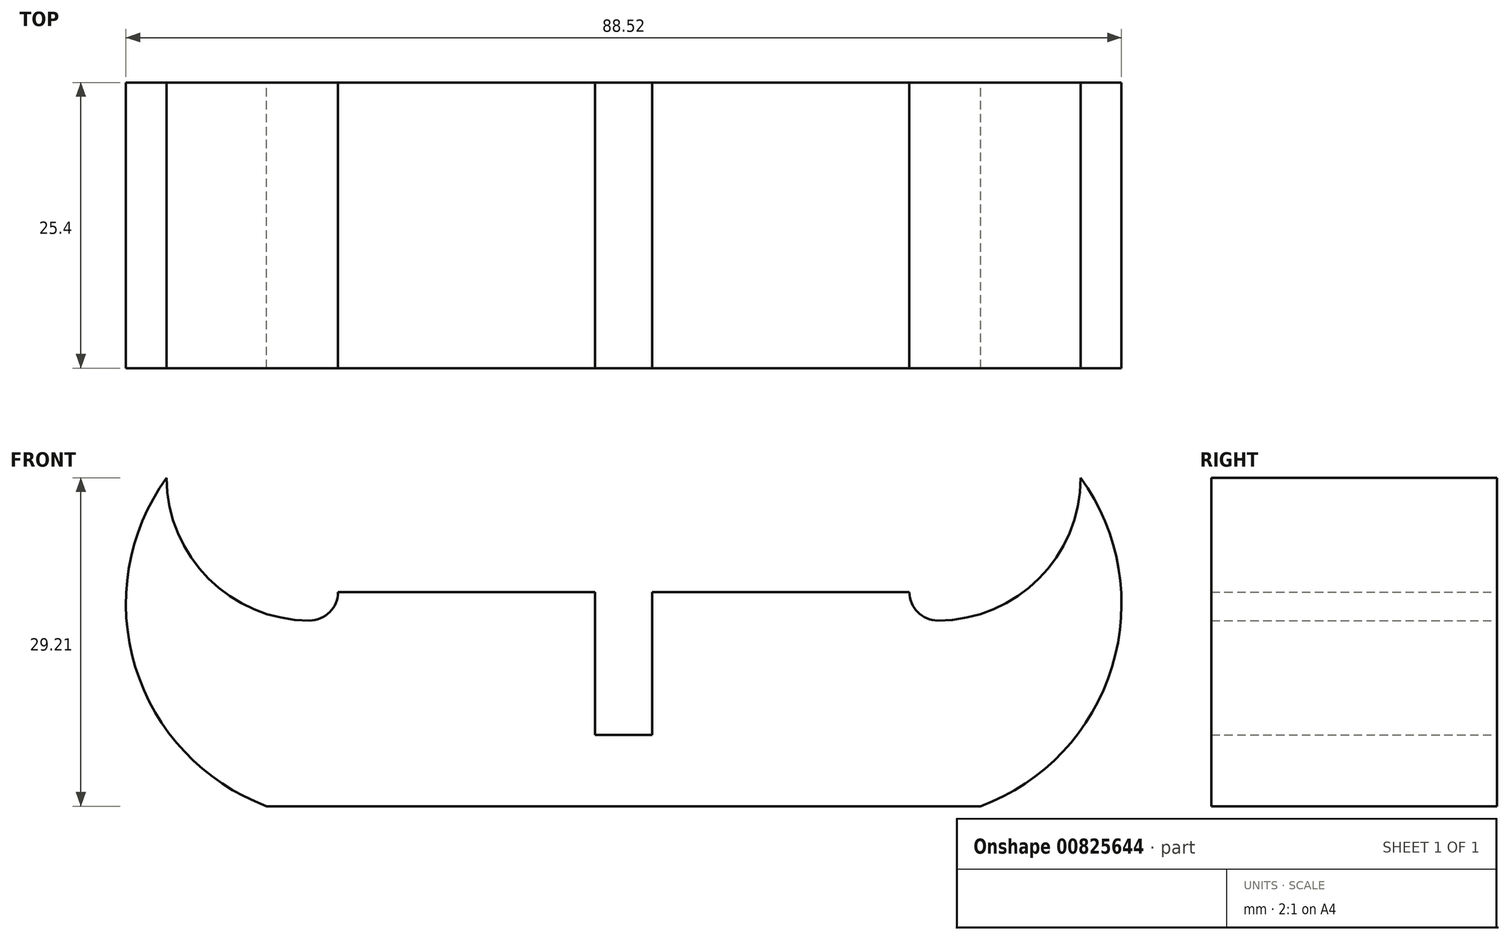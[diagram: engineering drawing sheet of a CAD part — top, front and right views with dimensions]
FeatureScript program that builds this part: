
annotation { "Feature Type Name" : "Feature", "Feature Type Description" : "" }
export const myFeature = defineFeature(function(context is Context, id is Id, definition is map)
    precondition{}
    {
        {
            var Q0;
            Q0=qCreatedBy(makeId("Front.planeOp"),FACE);
            var sketch = newSketch(context, id + "F0", { "sketchPlane" : qUnion([Q0])});
            skLineSegment(sketch, "E0", {"start": v(0, 0) * mm, "end": v(-19.05, 0) * mm});
            skLineSegment(sketch, "E1", {"start": v(-19.05, 0) * mm, "end": v(-19.05, -2.54) * mm});
            skLineSegment(sketch, "E2", {"start": v(-19.05, 0) * mm, "end": v(-25.4, 0) * mm});
            skLineSegment(sketch, "E3", {"start": v(0, 0) * mm, "end": v(0, -19.05) * mm});
            skPoint(sketch, "E4.endSnap0", {"position": v(-22.23, 0) * mm});
            skLineSegment(sketch, "E5", {"start": v(-25.4, -2.54) * mm, "end": v(-27.94, -2.54) * mm});
            skArc(sketch, "E6", {"start": v(-27.94, -2.54) * mm, "mid": v(-26.14, -1.8) * mm, "end": v(-25.4, 0) * mm});
            skLineSegment(sketch, "E7", {"start": v(-27.94, 0) * mm, "end": v(-27.94, 10.16) * mm});
            skLineSegment(sketch, "E8", {"start": v(-27.94, 10.16) * mm, "end": v(-40.64, 10.16) * mm});
            skArc(sketch, "E9", {"start": v(-40.64, 10.16) * mm, "mid": v(-36.92, 1.18) * mm, "end": v(-27.94, -2.54) * mm});
            skLineSegment(sketch, "E10", {"start": v(0, -19.05) * mm, "end": v(-31.75, -19.05) * mm});
            skArc(sketch, "E11", {"start": v(-40.64, 10.16) * mm, "mid": v(-43.43, -6.65) * mm, "end": v(-31.75, -19.05) * mm});
            skLineSegment(sketch, "E12", {"start": v(0, 0) * mm, "end": v(0, -12.7) * mm});
            skLineSegment(sketch, "E13.bottom", {"start": v(0, -12.7) * mm, "end": v(-2.54, -12.7) * mm});
            skLineSegment(sketch, "E13.top", {"start": v(0, 0) * mm, "end": v(-2.54, 0) * mm});
            skLineSegment(sketch, "E13.left", {"start": v(0, -12.7) * mm, "end": v(0, 0) * mm});
            skLineSegment(sketch, "E13.right", {"start": v(-2.54, -12.7) * mm, "end": v(-2.54, 0) * mm});
            skLineSegment(sketch, "E14.MirrorCS", {"start": v(0, -19.05) * mm, "end": v(31.75, -19.05) * mm});
            skLineSegment(sketch, "E15.MirrorCS", {"start": v(2.54, -12.7) * mm, "end": v(2.54, 0) * mm});
            skLineSegment(sketch, "E16.MirrorCS", {"start": v(0, -12.7) * mm, "end": v(2.54, -12.7) * mm});
            skLineSegment(sketch, "E17.MirrorCS", {"start": v(0, 0) * mm, "end": v(19.05, 0) * mm});
            skArc(sketch, "E18.MirrorCS", {"start": v(27.94, -2.54) * mm, "mid": v(26.14, -1.8) * mm, "end": v(25.4, 0) * mm});
            skArc(sketch, "E19.MirrorCS", {"start": v(40.64, 10.16) * mm, "mid": v(36.92, 1.18) * mm, "end": v(27.94, -2.54) * mm});
            skArc(sketch, "E20.MirrorCS", {"start": v(40.64, 10.16) * mm, "mid": v(43.43, -6.65) * mm, "end": v(31.75, -19.05) * mm});
            skLineSegment(sketch, "E21", {"start": v(19.05, 0) * mm, "end": v(25.4, 0) * mm});
            skSolve(sketch);
        }
        {
            var Q0;
            {var subQ2=sQuery(id+"F0.wireOp",EDGE,"E14.MirrorCS");Q0=makeQuery(id+"F0.imprint","IMPRINT",FACE,{"disambiguationData":[TD([[makeQuery(id+"F0.imprint","IMPRINT",EDGE,{"derivedFrom":subQ2}),1.0]])]});}
            var Q1;
            {var subQ3=sQuery(id+"F0.wireOp",EDGE,"E2");Q1=makeQuery(id+"F0.imprint","IMPRINT",FACE,{"disambiguationData":[TD([[makeQuery(id+"F0.imprint","IMPRINT",EDGE,{"derivedFrom":subQ3}),1.0]])]});}
            extrude(context, id + "F1", {"entities" : qUnion([Q0, Q1]), "depth" : 25.4 * mm, "offsetDistance" : 25.4 * mm});
        }
    });
